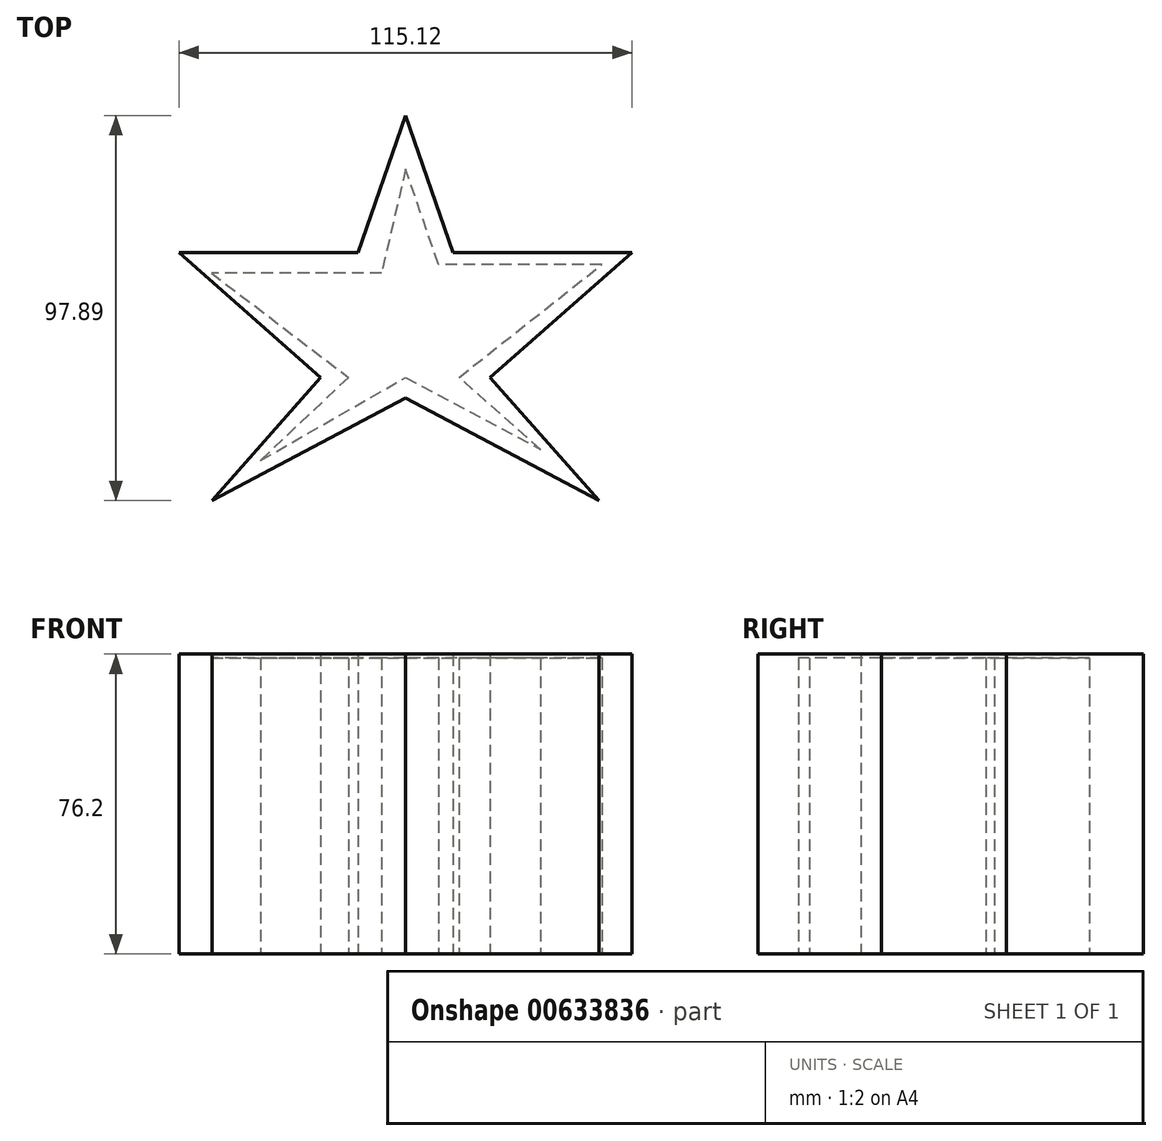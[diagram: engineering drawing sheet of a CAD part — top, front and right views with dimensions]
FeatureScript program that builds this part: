
annotation { "Feature Type Name" : "Feature", "Feature Type Description" : "" }
export const myFeature = defineFeature(function(context is Context, id is Id, definition is map)
    precondition{}
    {
        {
            var Q0;
            Q0=qCreatedBy(makeId("Top.planeOp"),FACE);
            var sketch = newSketch(context, id + "F0", { "sketchPlane" : qUnion([Q0])});
            skLineSegment(sketch, "E0", {"start": v(0, 49.93) * mm, "end": v(12.06, 15.12) * mm});
            skLineSegment(sketch, "E1", {"start": v(12.06, 15.12) * mm, "end": v(57.56, 15.12) * mm});
            skLineSegment(sketch, "E2", {"start": v(57.56, 15.12) * mm, "end": v(21.53, -16.64) * mm});
            skLineSegment(sketch, "E3", {"start": v(21.53, -16.64) * mm, "end": v(49.13, -47.96) * mm});
            skLineSegment(sketch, "E4", {"start": v(49.13, -47.96) * mm, "end": v(0, -21.83) * mm});
            skLineSegment(sketch, "E5.MirrorCS", {"start": v(-57.56, 15.12) * mm, "end": v(-21.53, -16.64) * mm});
            skLineSegment(sketch, "E6.MirrorCS", {"start": v(-12.06, 15.12) * mm, "end": v(-57.56, 15.12) * mm});
            skLineSegment(sketch, "E7.MirrorCS", {"start": v(-21.53, -16.64) * mm, "end": v(-49.13, -47.96) * mm});
            skLineSegment(sketch, "E8.MirrorCS", {"start": v(0, 49.93) * mm, "end": v(-12.06, 15.12) * mm});
            skLineSegment(sketch, "E9.MirrorCS", {"start": v(-49.13, -47.96) * mm, "end": v(0, -21.83) * mm});
            skSolve(sketch);
        }
        {
            var Q0;
            Q0=makeQuery(id+"F0.imprint","IMPRINT",FACE,{"disambiguationData":[TD([[makeQuery(id+"F0.imprint","IMPRINT",EDGE,{"derivedFrom":sQuery(id+"F0.wireOp",EDGE,"E0")}),-1.0]])]});
            extrude(context, id + "F1", {"entities" : qUnion([Q0]), "depth" : 76.2 * mm, "offsetDistance" : 25.4 * mm});
        }
        {
            var Q0;
            Q0=makeQuery(id+"F1.opExtrude","CAP_FACE",FACE,{"disambiguationData":[OSD([sQuery(id+"F0.wireOp",EDGE,"E0"),sQuery(id+"F0.wireOp",EDGE,"E1"),sQuery(id+"F0.wireOp",EDGE,"E2"),sQuery(id+"F0.wireOp",EDGE,"E3"),sQuery(id+"F0.wireOp",EDGE,"E4"),sQuery(id+"F0.wireOp",EDGE,"E5.MirrorCS"),sQuery(id+"F0.wireOp",EDGE,"E6.MirrorCS"),sQuery(id+"F0.wireOp",EDGE,"E7.MirrorCS"),sQuery(id+"F0.wireOp",EDGE,"E8.MirrorCS"),sQuery(id+"F0.wireOp",EDGE,"E9.MirrorCS")])],"isStart":false});
            var sketch = newSketch(context, id + "F2", { "sketchPlane" : qUnion([Q0])});
            skSolve(sketch);
        }
        {
            var Q0;
            Q0=qCreatedBy(makeId("Top.planeOp"),FACE);
            var sketch = newSketch(context, id + "F3", { "sketchPlane" : qUnion([Q0])});
            skLineSegment(sketch, "E10.0.0", {"start": v(0, 49.93) * mm, "end": v(-12.06, 15.12) * mm});
            skLineSegment(sketch, "E10.0.1", {"start": v(-12.06, 15.12) * mm, "end": v(-57.56, 15.12) * mm});
            skLineSegment(sketch, "E10.0.2", {"start": v(-57.56, 15.12) * mm, "end": v(-21.53, -16.64) * mm});
            skLineSegment(sketch, "E10.0.3", {"start": v(-21.53, -16.64) * mm, "end": v(-49.13, -47.96) * mm});
            skLineSegment(sketch, "E10.0.4", {"start": v(-49.13, -47.96) * mm, "end": v(0, -21.83) * mm});
            skLineSegment(sketch, "E10.0.5", {"start": v(0, -21.83) * mm, "end": v(49.13, -47.96) * mm});
            skLineSegment(sketch, "E10.0.6", {"start": v(49.13, -47.96) * mm, "end": v(21.53, -16.64) * mm});
            skLineSegment(sketch, "E10.0.7", {"start": v(21.53, -16.64) * mm, "end": v(57.56, 15.12) * mm});
            skLineSegment(sketch, "E10.0.8", {"start": v(57.56, 15.12) * mm, "end": v(12.06, 15.12) * mm});
            skLineSegment(sketch, "E10.0.9", {"start": v(12.06, 15.12) * mm, "end": v(0, 49.93) * mm});
            skPoint(sketch, "E11.endSnap0", {"position": v(-6.03, 32.52) * mm});
            skLineSegment(sketch, "E12", {"start": v(-6.03, 9.92) * mm, "end": v(-49.32, 9.92) * mm});
            skLineSegment(sketch, "E13", {"start": v(-49.32, 9.92) * mm, "end": v(-14.5, -16.64) * mm});
            skLineSegment(sketch, "E14", {"start": v(-14.5, -16.64) * mm, "end": v(-36.8, -37.71) * mm});
            skLineSegment(sketch, "E15", {"start": v(-36.8, -37.71) * mm, "end": v(0, -16.64) * mm});
            skLineSegment(sketch, "E16", {"start": v(0, -16.64) * mm, "end": v(34.33, -34.9) * mm});
            skPoint(sketch, "E16.endSnap0", {"position": v(-24.56, -34.9) * mm});
            skLineSegment(sketch, "E17", {"start": v(34.33, -34.9) * mm, "end": v(13.62, -16.64) * mm});
            skLineSegment(sketch, "E18", {"start": v(13.62, -16.64) * mm, "end": v(49.93, 12.06) * mm});
            skLineSegment(sketch, "E19", {"start": v(49.93, 12.06) * mm, "end": v(8.4, 12.06) * mm});
            skLineSegment(sketch, "E20", {"start": v(8.4, 12.06) * mm, "end": v(0, 36.3) * mm});
            skLineSegment(sketch, "E21", {"start": v(0, 36.3) * mm, "end": v(-6.03, 9.92) * mm});
            skSolve(sketch);
        }
        {
            var Q0;
            Q0=makeQuery(id+"F3.imprint","IMPRINT",FACE,{"disambiguationData":[TD([[makeQuery(id+"F3.imprint","IMPRINT",EDGE,{"derivedFrom":sQuery(id+"F3.wireOp",EDGE,"E12")}),1.0]])]});
            extrude(context, id + "F4", {"entities" : qUnion([Q0]), "operationType" : NewBodyOperationType.REMOVE, "depth" : 75.18 * mm, "offsetDistance" : 25.4 * mm});
        }
    });
